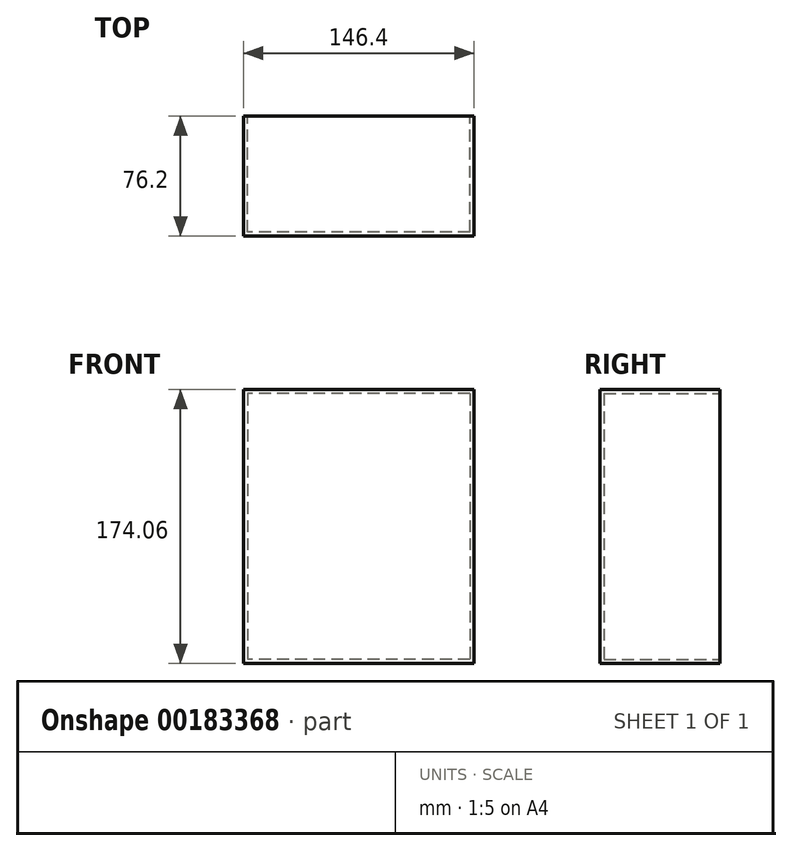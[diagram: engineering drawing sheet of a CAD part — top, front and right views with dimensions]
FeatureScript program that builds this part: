
annotation { "Feature Type Name" : "Feature", "Feature Type Description" : "" }
export const myFeature = defineFeature(function(context is Context, id is Id, definition is map)
    precondition{}
    {
        {
            var Q0;
            Q0=qCreatedBy(makeId("Front.planeOp"),FACE);
            var sketch = newSketch(context, id + "F0", { "sketchPlane" : qUnion([Q0])});
            skLineSegment(sketch, "E0.bottom", {"start": v(127.73, 83.68) * mm, "end": v(-127.73, 83.68) * mm});
            skLineSegment(sketch, "E0.top", {"start": v(127.73, -83.68) * mm, "end": v(-127.73, -83.68) * mm});
            skLineSegment(sketch, "E0.left", {"start": v(127.73, 83.68) * mm, "end": v(127.73, -83.68) * mm});
            skLineSegment(sketch, "E0.right", {"start": v(-127.73, 83.68) * mm, "end": v(-127.73, -83.68) * mm});
            skPoint(sketch, "E0.middle", {"position": v(0, 0) * mm});
            skSolve(sketch);
        }
        {
            var Q0;
            Q0=makeQuery(id+"F0.imprint","IMPRINT",FACE,{"disambiguationData":[TD([[makeQuery(id+"F0.imprint","IMPRINT",EDGE,{"derivedFrom":sQuery(id+"F0.wireOp",EDGE,"E0.bottom")}),1.0]])]});
            extrude(context, id + "F1", {"entities" : qUnion([Q0]), "depth" : 127 * mm});
        }
        {
            var Q0;
            Q0=makeQuery(id+"F1.opExtrude","SWEPT_BODY",BODY,{"disambiguationData":[OSD([sQuery(id+"F0.wireOp",EDGE,"E0.bottom"),sQuery(id+"F0.wireOp",EDGE,"E0.top"),sQuery(id+"F0.wireOp",EDGE,"E0.left"),sQuery(id+"F0.wireOp",EDGE,"E0.right")])]});
            deleteBodies(context, id + "F2", {"entities" : qUnion([Q0])});
        }
        {
            var Q0;
            Q0=qCreatedBy(makeId("Front.planeOp"),FACE);
            var sketch = newSketch(context, id + "F3", { "sketchPlane" : qUnion([Q0])});
            skLineSegment(sketch, "E1.bottom", {"start": v(73.2, 87.03) * mm, "end": v(-73.2, 87.03) * mm});
            skLineSegment(sketch, "E1.top", {"start": v(73.2, -87.03) * mm, "end": v(-73.2, -87.03) * mm});
            skLineSegment(sketch, "E1.left", {"start": v(73.2, 87.03) * mm, "end": v(73.2, -87.03) * mm});
            skLineSegment(sketch, "E1.right", {"start": v(-73.2, 87.03) * mm, "end": v(-73.2, -87.03) * mm});
            skPoint(sketch, "E1.middle", {"position": v(0, 0) * mm});
            skSolve(sketch);
        }
        {
            var Q0;
            Q0=makeQuery(id+"F3.imprint","IMPRINT",FACE,{"disambiguationData":[TD([[makeQuery(id+"F3.imprint","IMPRINT",EDGE,{"derivedFrom":sQuery(id+"F3.wireOp",EDGE,"E1.bottom")}),1.0]])]});
            extrude(context, id + "F4", {"entities" : qUnion([Q0]), "depth" : 76.2 * mm});
        }
        {
            var Q0;
            Q0=makeQuery(id+"F4.opExtrude","CAP_FACE",FACE,{"disambiguationData":[OSD([sQuery(id+"F3.wireOp",EDGE,"E1.bottom"),sQuery(id+"F3.wireOp",EDGE,"E1.top"),sQuery(id+"F3.wireOp",EDGE,"E1.left"),sQuery(id+"F3.wireOp",EDGE,"E1.right")])],"isStart":true});
            shell(context, id + "F5", {"entities" : qUnion([Q0]), "thickness" : 2.54 * mm});
        }
    });
